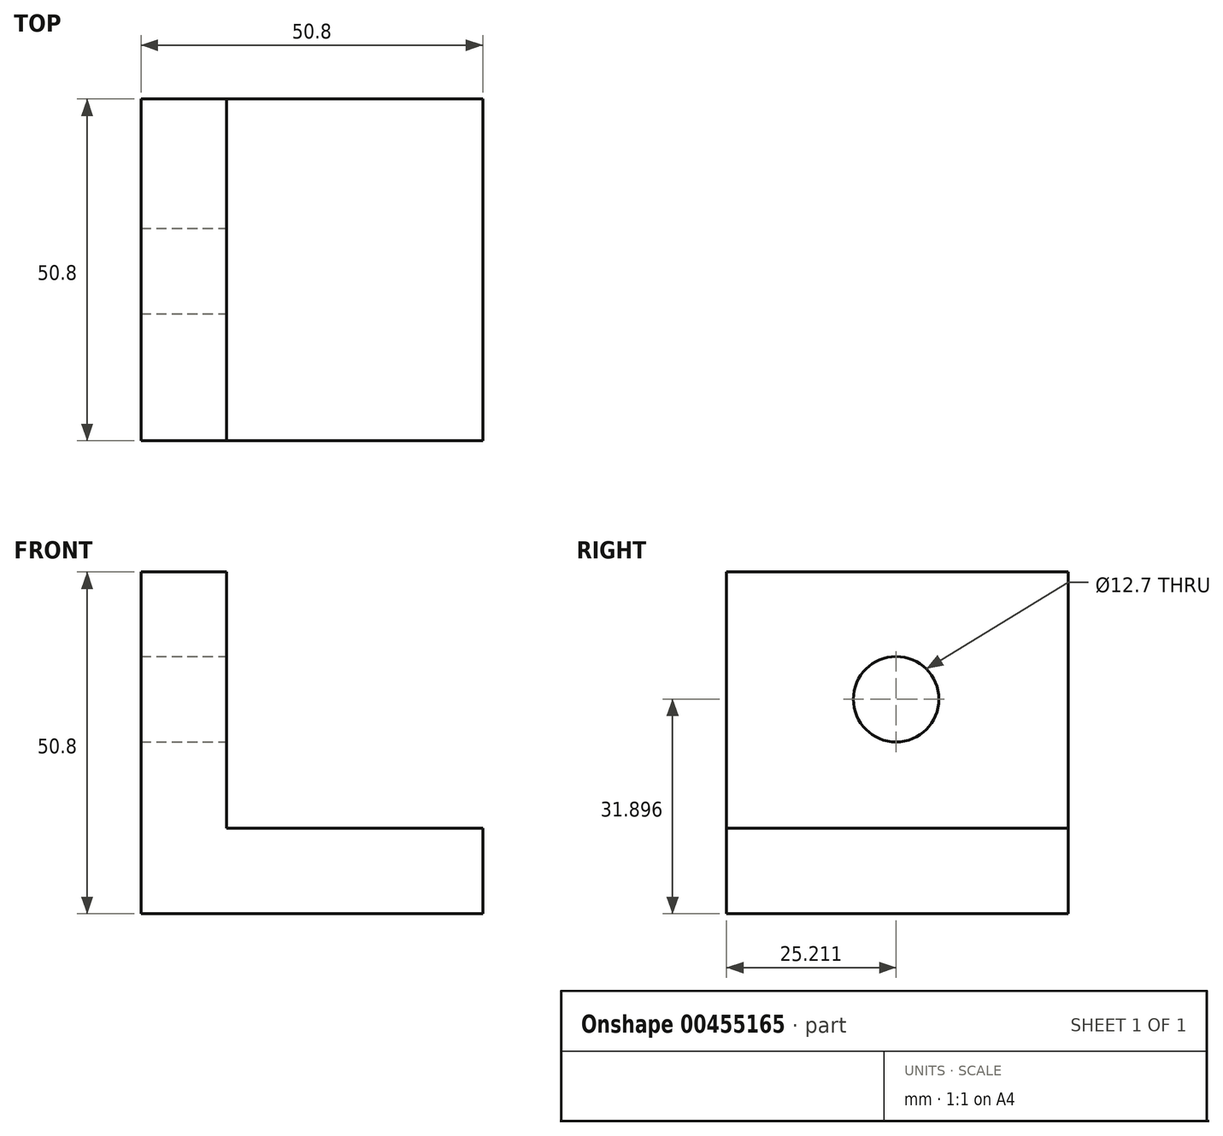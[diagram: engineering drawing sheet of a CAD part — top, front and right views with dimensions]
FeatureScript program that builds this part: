
annotation { "Feature Type Name" : "Feature", "Feature Type Description" : "" }
export const myFeature = defineFeature(function(context is Context, id is Id, definition is map)
    precondition{}
    {
        {
            var Q0;
            Q0=qCreatedBy(makeId("Top.planeOp"),FACE);
            var sketch = newSketch(context, id + "F0", { "sketchPlane" : qUnion([Q0])});
            skLineSegment(sketch, "E0.bottom", {"start": v(0, 0) * mm, "end": v(50.8, 0) * mm});
            skLineSegment(sketch, "E0.top", {"start": v(0, -50.8) * mm, "end": v(50.8, -50.8) * mm});
            skLineSegment(sketch, "E0.left", {"start": v(0, 0) * mm, "end": v(0, -50.8) * mm});
            skLineSegment(sketch, "E0.right", {"start": v(50.8, 0) * mm, "end": v(50.8, -50.8) * mm});
            skSolve(sketch);
        }
        {
            var Q0;
            Q0=makeQuery(id+"F0.imprint","IMPRINT",FACE,{"disambiguationData":[TD([[makeQuery(id+"F0.imprint","IMPRINT",EDGE,{"derivedFrom":sQuery(id+"F0.wireOp",EDGE,"E0.bottom")}),-1.0]])]});
            extrude(context, id + "F1", {"entities" : qUnion([Q0]), "depth" : 12.7 * mm});
        }
        {
            var Q0;
            Q0=qCreatedBy(makeId("Top.planeOp"),FACE);
            var sketch = newSketch(context, id + "F2", { "sketchPlane" : qUnion([Q0])});
            skLineSegment(sketch, "E1.bottom", {"start": v(0, 0) * mm, "end": v(12.7, 0) * mm});
            skLineSegment(sketch, "E1.top", {"start": v(0, -50.8) * mm, "end": v(12.7, -50.8) * mm});
            skLineSegment(sketch, "E1.left", {"start": v(0, 0) * mm, "end": v(0, -50.8) * mm});
            skLineSegment(sketch, "E1.right", {"start": v(12.7, 0) * mm, "end": v(12.7, -50.8) * mm});
            skSolve(sketch);
        }
        {
            var Q0;
            Q0 = qSketchRegion(id + "F2", true);
            extrude(context, id + "F3", {"entities" : qUnion([Q0]), "operationType" : NewBodyOperationType.ADD, "depth" : 50.8 * mm});
        }
        {
            var Q0;
            Q0=makeQuery(id+"F3.opExtrude","SWEPT_FACE",FACE,{"disambiguationData":[OSD([sQuery(id+"F2.wireOp",EDGE,"E1.right")])]});
            var sketch = newSketch(context, id + "F4", { "sketchPlane" : qUnion([Q0])});
            skSolve(sketch);
        }
        {
            var Q0;
            {var subQ0=sQuery(id+"F2.wireOp",EDGE,"E1.right");Q0=makeQuery(id+"F4.imprint","IMPRINT",FACE,{"disambiguationData":[TD([[makeQuery(id+"F4.imprint","IMPRINT",EDGE,{"derivedFrom":makeQuery(id+"F3.opExtrude","CAP_EDGE",EDGE,{"disambiguationData":[OSD([subQ0])],"isStart":false})}),1.0]])]});}
            var sketch = newSketch(context, id + "F5", { "sketchPlane" : qUnion([Q0])});
            skLineSegment(sketch, "E2", {"start": v(-25.59, 35.28) * mm, "end": v(-25.59, 28.5) * mm});
            skCircle(sketch, "E3", {"center": v(-25.59, 31.9) * mm, "radius": 6.35 * mm});
            skSolve(sketch);
        }
        {
            var Q0;
            Q0=sQuery(id+"F5.wireOp",VERTEX,"E3.center");
            var Q1;
            Q1=makeQuery(id+"F1.opExtrude","SWEPT_BODY",BODY,{"disambiguationData":[OSD([sQuery(id+"F0.wireOp",EDGE,"E0.bottom"),sQuery(id+"F0.wireOp",EDGE,"E0.top"),sQuery(id+"F0.wireOp",EDGE,"E0.left"),sQuery(id+"F0.wireOp",EDGE,"E0.right")])]});
            hole(context, id + "F6", {"style" : HoleStyle.SIMPLE, "endStyle" : HoleEndStyle.THROUGH, "holeDiameter" : 12.7 * mm, "isTappedThrough" : true, "tappedDepth" : 12.7 * mm, "tapClearance" : 3, "locations" : qUnion([Q0]), "scope" : qUnion([Q1])});
        }
    });
